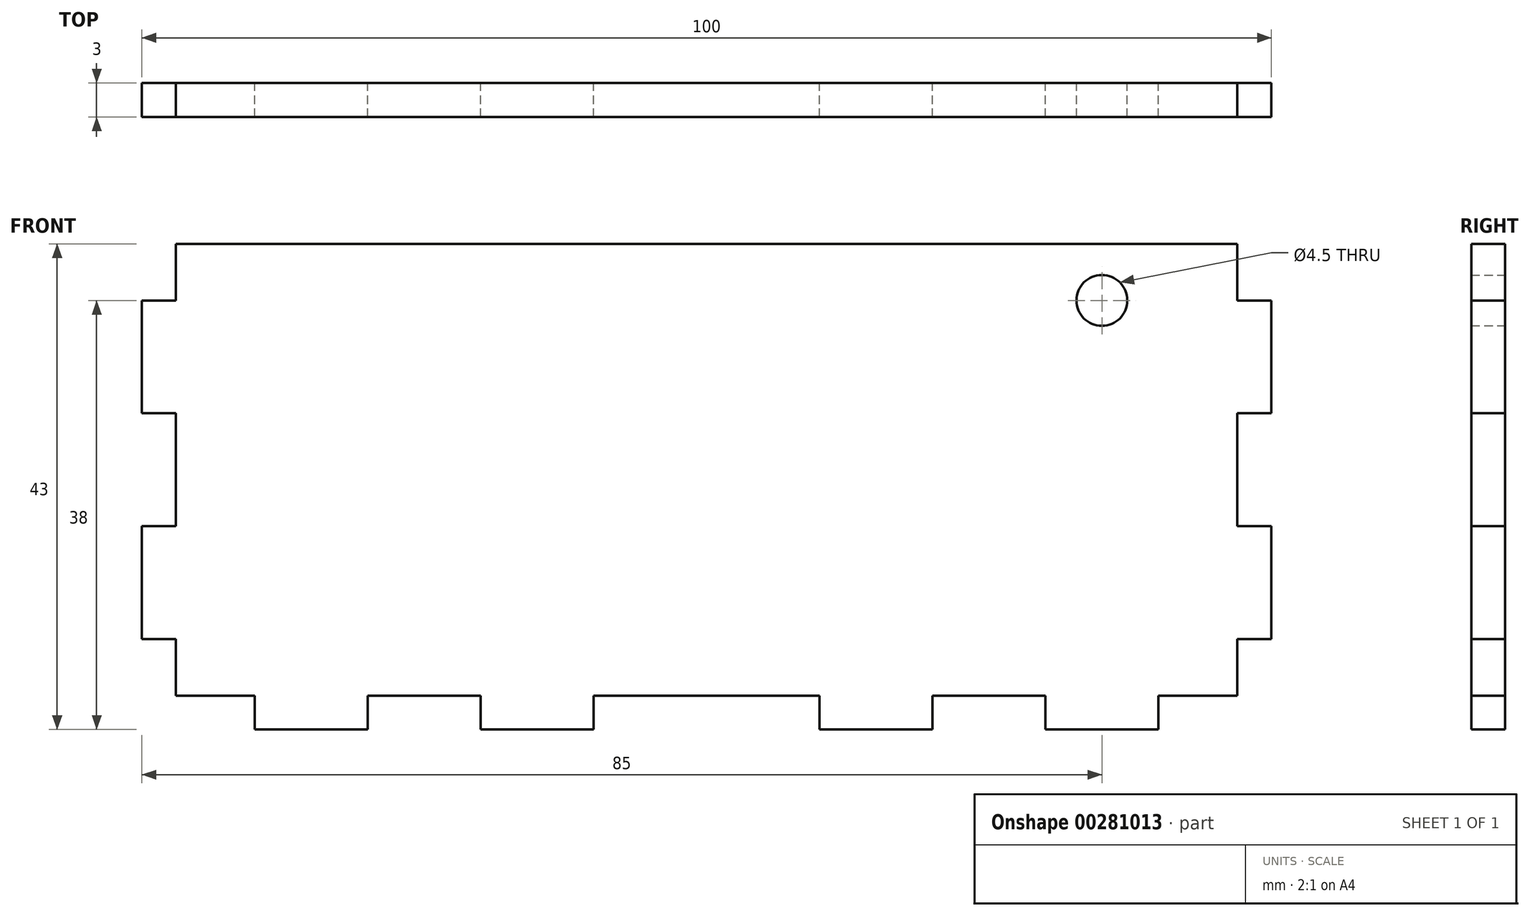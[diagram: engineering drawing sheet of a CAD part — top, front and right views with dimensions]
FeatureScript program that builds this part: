
annotation { "Feature Type Name" : "Feature", "Feature Type Description" : "" }
export const myFeature = defineFeature(function(context is Context, id is Id, definition is map)
    precondition{}
    {
        {
            var Q0;
            Q0=qCreatedBy(makeId("Front.planeOp"),FACE);
            var sketch = newSketch(context, id + "F0", { "sketchPlane" : qUnion([Q0])});
            skLineSegment(sketch, "E0.bottom", {"start": v(0, -20) * mm, "end": v(-10, -20) * mm});
            skLineSegment(sketch, "E0.top", {"start": v(47, 20) * mm, "end": v(-47, 20) * mm});
            skLineSegment(sketch, "E0.right", {"start": v(-50, -15) * mm, "end": v(-50, -5) * mm});
            skPoint(sketch, "E0.middle", {"position": v(0, 0) * mm});
            skLineSegment(sketch, "E1.top", {"start": v(-10, -23) * mm, "end": v(-20, -23) * mm});
            skLineSegment(sketch, "E1.left", {"start": v(-10, -20) * mm, "end": v(-10, -23) * mm});
            skLineSegment(sketch, "E1.right", {"start": v(-20, -20) * mm, "end": v(-20, -23) * mm});
            skLineSegment(sketch, "E2.top", {"start": v(-30, -23) * mm, "end": v(-40, -23) * mm});
            skLineSegment(sketch, "E2.left", {"start": v(-30, -20) * mm, "end": v(-30, -23) * mm});
            skLineSegment(sketch, "E2.right", {"start": v(-40, -20) * mm, "end": v(-40, -23) * mm});
            skPoint(sketch, "E3", {"position": v(0, -20) * mm});
            skLineSegment(sketch, "E4.trimOffspring", {"start": v(-20, -20) * mm, "end": v(-30, -20) * mm});
            skLineSegment(sketch, "E5.trimOffspring", {"start": v(-40, -20) * mm, "end": v(-47, -20) * mm});
            skLineSegment(sketch, "E6.MirrorCS", {"start": v(40, -20) * mm, "end": v(40, -23) * mm});
            skLineSegment(sketch, "E7.MirrorCS", {"start": v(30, -20) * mm, "end": v(30, -23) * mm});
            skLineSegment(sketch, "E8.MirrorCS", {"start": v(20, -20) * mm, "end": v(20, -23) * mm});
            skLineSegment(sketch, "E9.MirrorCS", {"start": v(10, -20) * mm, "end": v(10, -23) * mm});
            skLineSegment(sketch, "E10.MirrorCS", {"start": v(40, -20) * mm, "end": v(47, -20) * mm});
            skLineSegment(sketch, "E11.MirrorCS", {"start": v(20, -20) * mm, "end": v(30, -20) * mm});
            skLineSegment(sketch, "E12.MirrorCS", {"start": v(0, -20) * mm, "end": v(10, -20) * mm});
            skLineSegment(sketch, "E13.MirrorCS", {"start": v(10, -23) * mm, "end": v(20, -23) * mm});
            skLineSegment(sketch, "E14.MirrorCS", {"start": v(30, -23) * mm, "end": v(40, -23) * mm});
            skLineSegment(sketch, "E15.top", {"start": v(-50, 15) * mm, "end": v(-47, 15) * mm});
            skLineSegment(sketch, "E15.right", {"start": v(-47, 20) * mm, "end": v(-47, 15) * mm});
            skLineSegment(sketch, "E16.top", {"start": v(-50, -15) * mm, "end": v(-47, -15) * mm});
            skLineSegment(sketch, "E16.right", {"start": v(-47, -20) * mm, "end": v(-47, -15) * mm});
            skLineSegment(sketch, "E17.bottom", {"start": v(-50, 5) * mm, "end": v(-47, 5) * mm});
            skLineSegment(sketch, "E17.top", {"start": v(-50, -5) * mm, "end": v(-47, -5) * mm});
            skLineSegment(sketch, "E17.right", {"start": v(-47, 5) * mm, "end": v(-47, -5) * mm});
            skLineSegment(sketch, "E18.trimOffspring", {"start": v(-50, 5) * mm, "end": v(-50, 15) * mm});
            skPoint(sketch, "E19.orphan", {"position": v(-50, 20) * mm});
            skPoint(sketch, "E20.orphan", {"position": v(-50, -20) * mm});
            skPoint(sketch, "E0.left.start.orphan", {"position": v(50, -20) * mm});
            skLineSegment(sketch, "E21.MirrorCS", {"start": v(50, -15) * mm, "end": v(47, -15) * mm});
            skLineSegment(sketch, "E22.MirrorCS", {"start": v(50, -5) * mm, "end": v(47, -5) * mm});
            skLineSegment(sketch, "E23.MirrorCS", {"start": v(50, 15) * mm, "end": v(47, 15) * mm});
            skLineSegment(sketch, "E24.MirrorCS", {"start": v(50, 5) * mm, "end": v(47, 5) * mm});
            skLineSegment(sketch, "E25.MirrorCS", {"start": v(50, 5) * mm, "end": v(50, 15) * mm});
            skLineSegment(sketch, "E26.MirrorCS", {"start": v(47, -20) * mm, "end": v(47, -15) * mm});
            skLineSegment(sketch, "E27.MirrorCS", {"start": v(50, -15) * mm, "end": v(50, -5) * mm});
            skLineSegment(sketch, "E28.MirrorCS", {"start": v(47, 5) * mm, "end": v(47, -5) * mm});
            skLineSegment(sketch, "E29.MirrorCS", {"start": v(47, 20) * mm, "end": v(47, 15) * mm});
            skPoint(sketch, "E30.orphan", {"position": v(50, 20) * mm});
            skCircle(sketch, "E31", {"center": v(35, 15) * mm, "radius": 2.25 * mm});
            skSolve(sketch);
        }
        {
            var Q0;
            Q0 = qSketchRegion(id + "F0", true);
            extrude(context, id + "F1", {"entities" : qUnion([Q0]), "depth" : 3 * mm});
        }
    });
